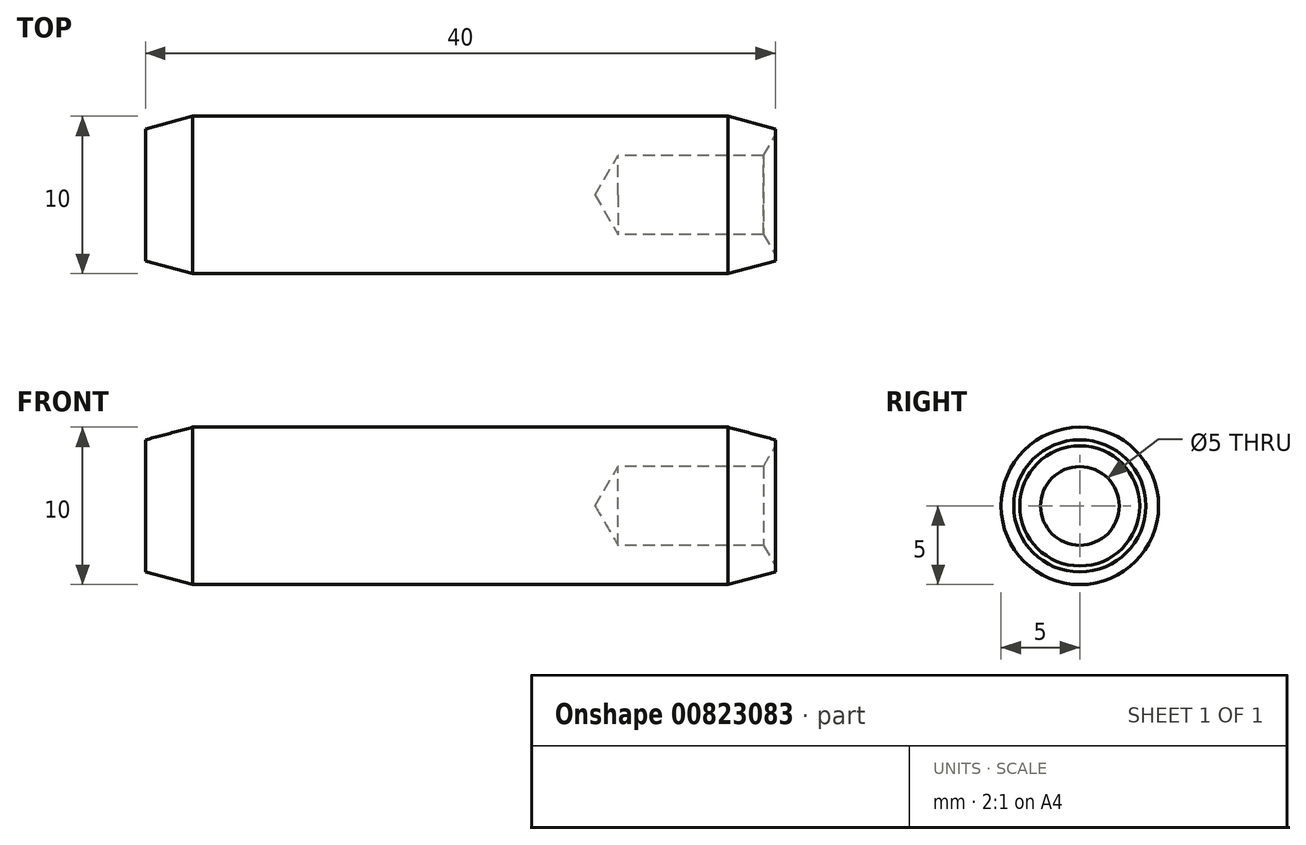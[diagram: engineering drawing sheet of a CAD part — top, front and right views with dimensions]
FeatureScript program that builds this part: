
annotation { "Feature Type Name" : "Feature", "Feature Type Description" : "" }
export const myFeature = defineFeature(function(context is Context, id is Id, definition is map)
    precondition{}
    {
        {
            var Q0;
            Q0=qCreatedBy(makeId("Front.planeOp"),FACE);
            var sketch = newSketch(context, id + "F0", { "sketchPlane" : qUnion([Q0])});
            skLineSegment(sketch, "E0", {"start": v(0, 0) * mm, "end": v(6.76, 0) * mm, "construction": true});
            skLineSegment(sketch, "E1", {"start": v(1.44, 2.5) * mm, "end": v(0, 0) * mm});
            skLineSegment(sketch, "E2", {"start": v(1.44, 2.5) * mm, "end": v(10.69, 2.5) * mm});
            skLineSegment(sketch, "E3", {"start": v(10.69, 2.5) * mm, "end": v(11.44, 3.81) * mm});
            skLineSegment(sketch, "E4", {"start": v(11.44, 3.81) * mm, "end": v(11.44, 4.2) * mm});
            skLineSegment(sketch, "E5", {"start": v(11.44, 4.2) * mm, "end": v(8.44, 5) * mm});
            skLineSegment(sketch, "E6", {"start": v(8.44, 5) * mm, "end": v(-25.56, 5) * mm});
            skLineSegment(sketch, "E7", {"start": v(-25.56, 5) * mm, "end": v(-28.56, 4.2) * mm});
            skLineSegment(sketch, "E8", {"start": v(-28.56, 4.2) * mm, "end": v(-28.56, 0) * mm});
            skLineSegment(sketch, "E9", {"start": v(-28.56, 0) * mm, "end": v(0, 0) * mm});
            skSolve(sketch);
        }
        {
            var Q0;
            Q0=makeQuery(id+"F0.imprint","IMPRINT",FACE,{"disambiguationData":[TD([[makeQuery(id+"F0.imprint","IMPRINT",EDGE,{"derivedFrom":sQuery(id+"F0.wireOp",EDGE,"E1")}),-1.0]])]});
            var Q1;
            Q1=sQuery(id+"F0.wireOp",EDGE,"E0");
            revolve(context, id + "F1", {"surfaceOperationType" : NewSurfaceOperationType.NEW, "entities" : qUnion([Q0]), "axis" : qUnion([Q1]), "revolveType" : RevolveType.FULL});
        }
    });
